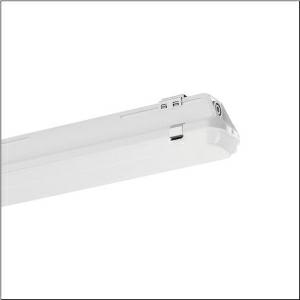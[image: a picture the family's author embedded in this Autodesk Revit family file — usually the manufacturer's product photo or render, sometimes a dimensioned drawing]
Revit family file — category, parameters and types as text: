
# Revit family: monsun_11_51fp10dp660l
name_source: partatom
category: Lighting Fixtures
units: mm (PartAtom-declared; Revit-internal decimal feet)

## family parameters
Cut with Voids When Loaded = No
Host = Face
Light Source = No
Part Type = Normal
Room Calculation Point = No
Round Connector Dimension = Use Diameter
Shared = No

## types (1)
- --- (1 x LED, 5970 lm, 34.1 W, 6500K)
    Apparent Load = 34 VA
    CIE Flux Codes = 47 77 93 94 100
    Color Rendering = 80
    Color Temperature = 6500K
    Default Elevation = 1800 mm
    Description = Monsun 11, damp-proof luminaire, chain hanger, primary optical cover: enclosure, of PMMA, light emission: direct distribution, primary light characteristic: symmetric, installation type: suspended mounting, surface-mounted, horizontal mounting, vertical mounting, LED, rated luminous flux: 5.970lm, luminous efficacy: 192lm/W, light colour: 865, colour temperature: 6500K, control gear: DALI 2, with terminal, 5-pole, max. 2.5mm², mains connection: 220..240V, AC, 50/60Hz, rated input power: 31W, luminaire housing, of glass-fibre reinforced polyester, uncoated, bright grey, incl. chain hanger, length: 1.590mm, width: 90mm, height: 88mm, clip for enclosure, of stainless steel (V2A), ceiling mounting element, of stainless steel (V2A), chain hanger, of stainless steel (V2A), protection rating (complete): IP66, insulation class (complete): insulation class I (protective earthing), certification: CE, ENEC, VDE, UKCA, protection symbol: D, impact resistance: IK04, permissible operating ambient temperature: -25..+35°C, standard: EN 50419, EN 60598-2-1, corresponds to IFS (International Featured Standards) requirements for safety and quality in the food industry, for indoor or canopied outdoor use, no direct snow, no direct sun, no direct rain, LABS conformity tested according to VDMA 24364:2018-05, contact your sales advisor before using the luminaires in applications with unclear chemical exposure, large temperature fluctuations or condensation-forming humidity, packaging unit: 1 piece
    Height = 89 mm
    Lamp = 1 x LED
    Lamp Light Flux = 5970 lm
    Lamp Power = 34.1 W
    Lamp count = 1
    Length = 1590 mm
    Luminous efficacy = 175 lm/W
    Manufacturer = Siteco
    ModVariant = No
    Model = 51FP10DP660L
    Mounting Place = Ceiling
    Mounting Type = Surface mounted
    Number of Poles = 1
    OnlyDefault = Yes
    Power Factor = 1
    Product Name = Monsun 11
    Product group = damp-proof luminaire
    ProductGroupID = 300
    Protection Class = Protection class I
    Protection Degree = IP 66
    RLX_Detail_Level = 1
    RLX_Emergency_Light_Flux = 0 lm
    RLX_Emergency_Type = 0
    RLX_Emergency_Type_DB = No
    RlxData = <blob elided: 92153 chars, md5=a5ba4873>
    Socket = socket
    Standby Power = 0 W
    System Light Flux = 5970 lm
    System Power = 34 W
    Type Comments = factory setting: luminous flux: 100 % | dim-lin: 254 | 237 mA
    Type Image = l_1349237.jpg
    URL = http://relux.com
    VarID = @adj_015481
    Voltage = 0 V
    Weight = 0.00 kg
    Width = 90 mm

## geometry (parser evidence)
native form markers: Blend x4, Sweep x13
no freeform markers — native parametric forms only
